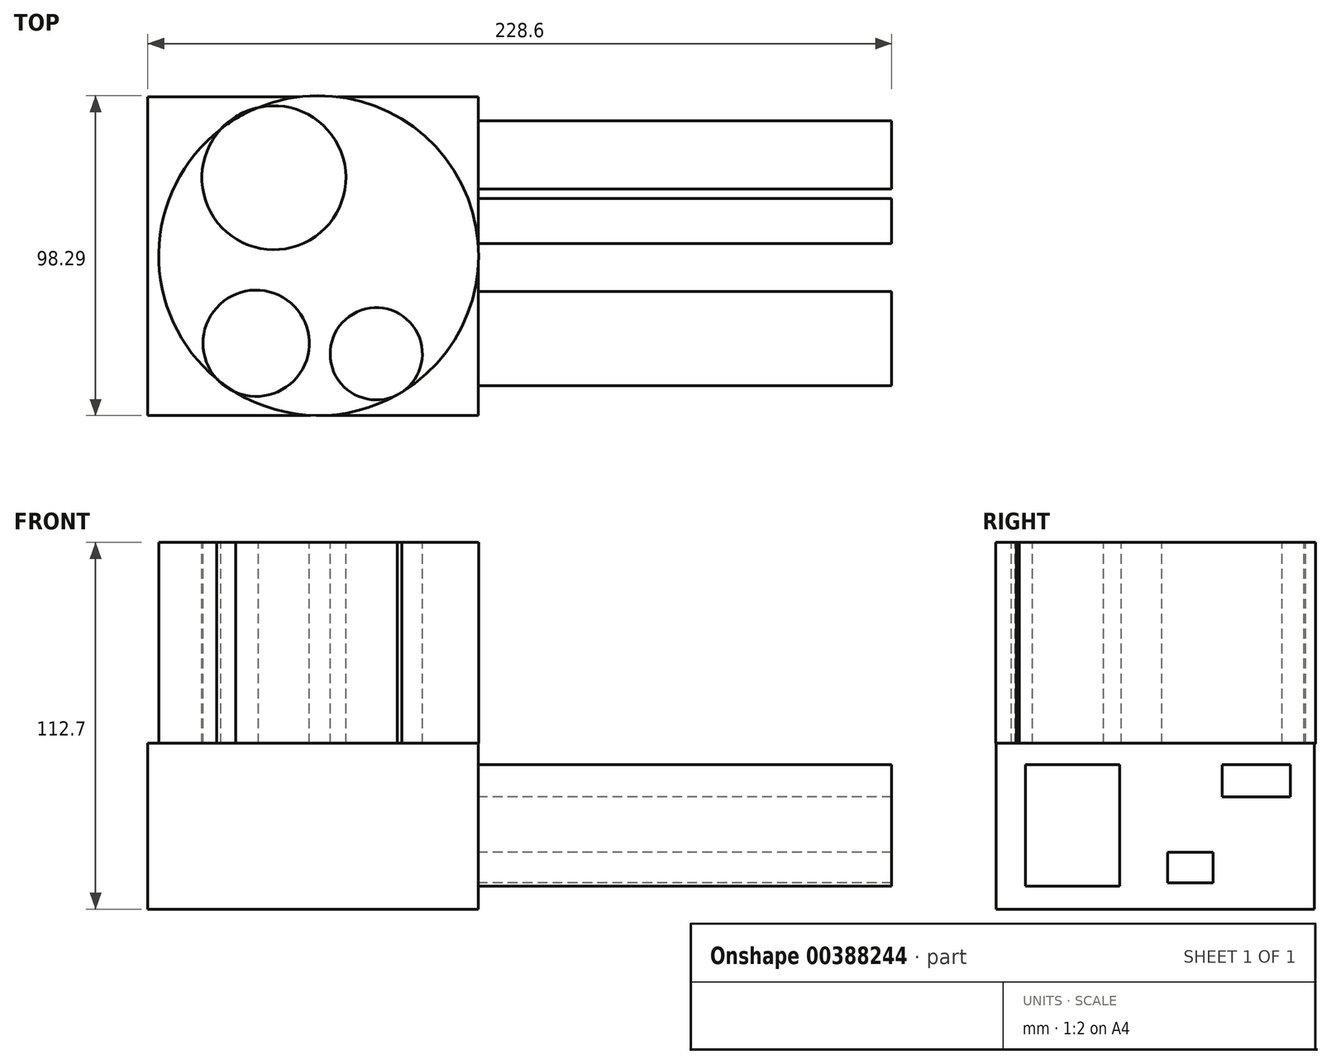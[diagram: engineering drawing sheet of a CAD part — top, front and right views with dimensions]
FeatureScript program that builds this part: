
annotation { "Feature Type Name" : "Feature", "Feature Type Description" : "" }
export const myFeature = defineFeature(function(context is Context, id is Id, definition is map)
    precondition{}
    {
        {
            var Q0;
            Q0=qCreatedBy(makeId("Top.planeOp"),FACE);
            var sketch = newSketch(context, id + "F0", { "sketchPlane" : qUnion([Q0])});
            skCircle(sketch, "E0", {"center": v(1.7, 2.55) * mm, "radius": 49.15 * mm});
            skPoint(sketch, "E0.first.point", {"position": v(-28.37, 41.42) * mm});
            skPoint(sketch, "E0.second.point", {"position": v(27.24, -39.44) * mm});
            skPoint(sketch, "E0.third.point", {"position": v(-23.83, -39.44) * mm});
            skCircle(sketch, "E1", {"center": v(19.41, -27.62) * mm, "radius": 14.17 * mm});
            skPoint(sketch, "E1.second.point", {"position": v(11.07, -16.17) * mm});
            skPoint(sketch, "E1.third.point", {"position": v(24.68, -14.47) * mm});
            skCircle(sketch, "E2", {"center": v(-17.5, -24.39) * mm, "radius": 16.33 * mm});
            skPoint(sketch, "E2.second.point", {"position": v(-19.86, -8.23) * mm});
            skPoint(sketch, "E2.third.point", {"position": v(-33.76, -22.98) * mm});
            skCircle(sketch, "E3", {"center": v(-12.06, 26.49) * mm, "radius": 22.12 * mm});
            skPoint(sketch, "E3.second.point", {"position": v(0, 7.94) * mm});
            skPoint(sketch, "E3.third.point", {"position": v(4.26, 41.42) * mm});
            skSolve(sketch);
        }
        {
            var Q0;
            {var subQ0=sQuery(id+"F0.wireOp",EDGE,"E3");var subQ1=sQuery(id+"F0.wireOp",EDGE,"E0");var subQ2=makeQuery(id+"F0.imprint","INTERSECT",VERTEX,{"disambiguationData":[OD(0.0)],"derivedFrom":[subQ1,subQ0]});Q0=makeQuery(id+"F0.imprint","IMPRINT",FACE,{"disambiguationData":[TD([[makeQuery(id+"F0.imprint","IMPRINT",EDGE,{"disambiguationData":[TD([[subQ2,1.0]])],"derivedFrom":subQ1}),-1.0]])]});}
            var Q1;
            {var subQ0=sQuery(id+"F0.wireOp",EDGE,"E2");var subQ1=sQuery(id+"F0.wireOp",EDGE,"E0");var subQ2=makeQuery(id+"F0.imprint","INTERSECT",VERTEX,{"disambiguationData":[OD(0.0)],"derivedFrom":[subQ1,subQ0]});Q1=makeQuery(id+"F0.imprint","IMPRINT",FACE,{"disambiguationData":[TD([[makeQuery(id+"F0.imprint","IMPRINT",EDGE,{"disambiguationData":[TD([[subQ2,-1.0]])],"derivedFrom":subQ1}),-1.0]])]});}
            var Q2;
            {var subQ0=sQuery(id+"F0.wireOp",EDGE,"E1");var subQ1=sQuery(id+"F0.wireOp",EDGE,"E0");var subQ2=makeQuery(id+"F0.imprint","INTERSECT",VERTEX,{"disambiguationData":[OD(0.0)],"derivedFrom":[subQ1,subQ0]});Q2=makeQuery(id+"F0.imprint","IMPRINT",FACE,{"disambiguationData":[TD([[makeQuery(id+"F0.imprint","IMPRINT",EDGE,{"disambiguationData":[TD([[subQ2,-1.0]])],"derivedFrom":subQ1}),-1.0]])]});}
            var Q3;
            {var subQ1=sQuery(id+"F0.wireOp",EDGE,"E0");var subQ4=sQuery(id+"F0.wireOp",EDGE,"E3");var subQ8=makeQuery(id+"F0.imprint","INTERSECT",VERTEX,{"disambiguationData":[OD(0.0)],"derivedFrom":[subQ1,subQ4]});Q3=makeQuery(id+"F0.imprint","IMPRINT",FACE,{"disambiguationData":[TD([[makeQuery(id+"F0.imprint","IMPRINT",EDGE,{"disambiguationData":[TD([[subQ8,-1.0]])],"derivedFrom":subQ1}),1.0]])]});}
            extrude(context, id + "F1", {"entities" : qUnion([Q0, Q1, Q2, Q3]), "depth" : 61.72 * mm, "hasDraft" : true, "draftAngle" : 0 * degree});
        }
        {
            var Q0;
            Q0=qCreatedBy(makeId("Right.planeOp"),FACE);
            var sketch = newSketch(context, id + "F2", { "sketchPlane" : qUnion([Q0])});
            skLineSegment(sketch, "E4.bottom", {"start": v(51.35, 0) * mm, "end": v(-46.53, 0) * mm});
            skLineSegment(sketch, "E4.top", {"start": v(51.35, -50.98) * mm, "end": v(-46.53, -50.98) * mm});
            skLineSegment(sketch, "E4.left", {"start": v(51.35, 0) * mm, "end": v(51.35, -50.98) * mm});
            skLineSegment(sketch, "E4.right", {"start": v(-46.53, 0) * mm, "end": v(-46.53, -50.98) * mm});
            skSolve(sketch);
        }
        {
            var Q0;
            Q0 = qSketchRegion(id + "F2", true);
            extrude(context, id + "F3", {"entities" : qUnion([Q0]), "endBound" : BoundingType.SYMMETRIC, "depth" : 101.6 * mm});
        }
        {
            var Q0;
            Q0=makeQuery(id+"F3.opExtrude","CAP_FACE",FACE,{"disambiguationData":[OSD([sQuery(id+"F2.wireOp",EDGE,"E4.bottom"),sQuery(id+"F2.wireOp",EDGE,"E4.top"),sQuery(id+"F2.wireOp",EDGE,"E4.left"),sQuery(id+"F2.wireOp",EDGE,"E4.right")])],"isStart":false});
            var sketch = newSketch(context, id + "F4", { "sketchPlane" : qUnion([Q0])});
            skLineSegment(sketch, "E5.bottom", {"start": v(-37.45, -43.98) * mm, "end": v(-8.51, -43.98) * mm});
            skLineSegment(sketch, "E5.top", {"start": v(-37.45, -6.53) * mm, "end": v(-8.51, -6.53) * mm});
            skLineSegment(sketch, "E5.left", {"start": v(-37.45, -43.98) * mm, "end": v(-37.45, -6.53) * mm});
            skLineSegment(sketch, "E5.right", {"start": v(-8.51, -43.98) * mm, "end": v(-8.51, -6.53) * mm});
            skLineSegment(sketch, "E6.bottom", {"start": v(6.24, -42.84) * mm, "end": v(20.14, -42.84) * mm});
            skLineSegment(sketch, "E6.top", {"start": v(6.24, -33.48) * mm, "end": v(20.14, -33.48) * mm});
            skLineSegment(sketch, "E6.left", {"start": v(6.24, -42.84) * mm, "end": v(6.24, -33.48) * mm});
            skLineSegment(sketch, "E6.right", {"start": v(20.14, -42.84) * mm, "end": v(20.14, -33.48) * mm});
            skLineSegment(sketch, "E7.bottom", {"start": v(22.98, -16.46) * mm, "end": v(43.98, -16.46) * mm});
            skLineSegment(sketch, "E7.top", {"start": v(22.98, -6.53) * mm, "end": v(43.98, -6.53) * mm});
            skLineSegment(sketch, "E7.left", {"start": v(22.98, -16.46) * mm, "end": v(22.98, -6.53) * mm});
            skLineSegment(sketch, "E7.right", {"start": v(43.98, -16.46) * mm, "end": v(43.98, -6.53) * mm});
            skSolve(sketch);
        }
        {
            var Q0;
            Q0=makeQuery(id+"F4.imprint","IMPRINT",FACE,{"disambiguationData":[TD([[makeQuery(id+"F4.imprint","IMPRINT",EDGE,{"derivedFrom":sQuery(id+"F4.wireOp",EDGE,"E7.bottom")}),1.0]])]});
            var Q1;
            Q1=makeQuery(id+"F4.imprint","IMPRINT",FACE,{"disambiguationData":[TD([[makeQuery(id+"F4.imprint","IMPRINT",EDGE,{"derivedFrom":sQuery(id+"F4.wireOp",EDGE,"E6.bottom")}),1.0]])]});
            var Q2;
            Q2=makeQuery(id+"F4.imprint","IMPRINT",FACE,{"disambiguationData":[TD([[makeQuery(id+"F4.imprint","IMPRINT",EDGE,{"derivedFrom":sQuery(id+"F4.wireOp",EDGE,"E5.bottom")}),1.0]])]});
            extrude(context, id + "F5", {"entities" : qUnion([Q0, Q1, Q2]), "operationType" : NewBodyOperationType.ADD, "depth" : 127 * mm});
        }
    });
